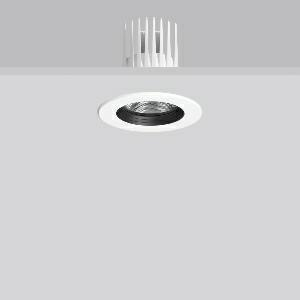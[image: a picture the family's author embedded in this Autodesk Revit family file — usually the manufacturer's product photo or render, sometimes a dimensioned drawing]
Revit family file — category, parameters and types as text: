
# Revit family: heledon_mini_e_901741_002_1_76_6f4a
name_source: partatom
category: Lighting Fixtures
units: mm (PartAtom-declared; Revit-internal decimal feet)

## family parameters
Cut with Voids When Loaded = No
Host = Face
Light Source = No
Part Type = Normal
Room Calculation Point = No
Round Connector Dimension = Use Diameter
Shared = No

## types (1)
- HELEDON mini E (1 x LED Modul 940, 2600 lm, 4000)
    Apparent Load = 20 VA
    Approval mark = CE
    CIE Flux Codes = 99 100 100 100 100
    Color Rendering = 92
    Color Temperature = 4000
    Default Elevation = 1800 mm
    Description = Series: HELEDON mini
Round recessed downlight. Housing: die-cast aluminium, powder-coated. Black plastic ring and recessed LED to prevent glare from the side. Optical assembly with reflector made of MIRO-Silver with 98% total light reflection for outstanding efficiency - can be changed without tools. Best colour rendering index Ra>90. Suitable for Recessed ceiling mounting. Installation without tools thanks to spring fastening system. Including separate LED converter with connecting cable 600 mm.High quality converter without flickering and stroboscopic effect. Through-wiring box (5 pole) available as accessory. The following accessories can be mounted without use of tools: interchangeable lenses, decorative glasses, honeycomb louvre, clear and frosted diffusers, white interchangeable plastic ring. 
Colour: traffic white, matt (RAL 9016)
Diameter: 124 mm
Height: 3 mm
Cut-out diameter: 114 mm
Recess height: 170 mm
Luminaire: recess height: 120 mm
Lamp: LED
Socket: without socket
Colour temperature: 4000K
Colour rendering index (CRI): 92
System power: 20 W
Rated luminous flux: 2600 lm
Luminous efficiency: 130 lm/W
Control gear: Converter, dimmable, DALI
Protection class: II
Type of protection: IP 20
    Height = 0 mm  [stored 0 ft]
    Lamp = 1 x LED Modul 940
    Lamp Light Flux = 2600 lm
    Lamp count = 1
    Length = 124 mm  [stored 0.406824 ft]
    Lifetime = 50000 h
    Luminous efficacy = 130 lm/W
    Manufacturer = RZB
    ModVariant = No
    Model = 901741.002.1.76
    Mounting Place = Ceiling
    Mounting Type = Recessed
    Number of Poles = 1
    OnlyDefault = Yes
    Power Factor = 1
    Product Name = HELEDON mini E
    Product group = Recessed downlights
    ProductGroupID = 402
    Protection Class = Protection class II
    Protection Degree = IP 20
    RLX_Detail_Level = 1
    RLX_Emergency_Light_Flux = 0 lm
    RLX_Emergency_Type = 0
    RLX_Emergency_Type_DB = No
    RlxData = <blob elided: 127733 chars, md5=aa2ea510>
    Socket = socket
    Standby Power = 0 W
    System Light Flux = 2600 lm
    System Power = 20 W
    Type Comments = Product without accessories
    Type Image = 901657.002.jpg
    URL = http://relux.com
    VarID = ---
    Voltage = 230 V
    Voltage Range = 220-240 V
    Weight = 0.00 kg
    Width = 0 mm  [stored 0 ft]

note: [stored X ft] marks values corroborated as IEEE doubles in the binary element streams (Revit-internal decimal feet)

## geometry (parser evidence)
native form markers: Blend x4, Sweep x11
no freeform markers — native parametric forms only
